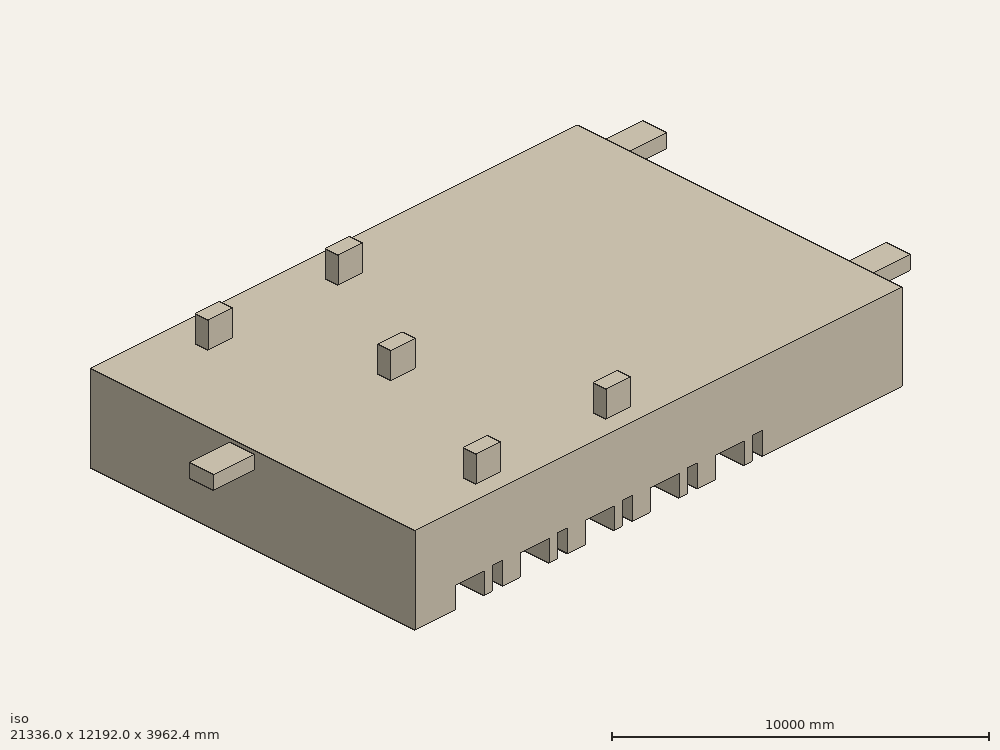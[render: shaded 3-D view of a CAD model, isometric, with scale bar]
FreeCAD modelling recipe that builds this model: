
FCSTD DOCUMENT  (FreeCAD 0.18R14555 (Git shallow))
Label: flow_domain
License: All rights reserved
LicenseURL: http://en.wikipedia.org/wiki/All_rights_reserved
objects: Part::Box×20, Part::MultiFuse×12, Part::Mirroring×1, Part::Cut×1
note: 34 computed .brp shape members not serialized (recipe doc carries the construction recipe); baked Part::Feature solids carry a one-line shape summary decoded from their .brp

FEATURE [Part::Box] Box001  label="Bed 1"
  AttacherType = Attacher::AttachEngine3D
  Height = 762
  Length = 1066.8
  Width = 1981.2
FEATURE [Part::Box] Box002  label="Table 1"
  AttacherType = Attacher::AttachEngine3D
  Height = 798.576
  Length = 396.24
  Placement = pos=(1371.6,0,0) rot=(0,0,1;0rad)
  Width = 396.24
FEATURE [Part::MultiFuse] Fusion  label="Set 1"
  Shapes = -> [Box002,Box001]
FEATURE [Part::Box] Box003  label="Bed 002"
  AttacherType = Attacher::AttachEngine3D
  Height = 762
  Length = 1066.8
  Width = 1981.2
FEATURE [Part::Box] Box004  label="Table 002"
  AttacherType = Attacher::AttachEngine3D
  Height = 798.576
  Length = 396.24
  Placement = pos=(1371.6,0,0) rot=(0,0,1;0rad)
  Width = 396.24
FEATURE [Part::MultiFuse] Fusion001  label="Set 2"
  Placement = pos=(2438.4,0,0) rot=(0,0,1;0rad)
  Shapes = -> [Box004,Box003]
FEATURE [Part::Box] Box005  label="Table 003"
  AttacherType = Attacher::AttachEngine3D
  Height = 798.576
  Length = 396.24
  Placement = pos=(1371.6,0,0) rot=(0,0,1;0rad)
  Width = 396.24
FEATURE [Part::Box] Box006  label="Bed 003"
  AttacherType = Attacher::AttachEngine3D
  Height = 762
  Length = 1066.8
  Width = 1981.2
FEATURE [Part::MultiFuse] Fusion002  label="Set 3"
  Placement = pos=(4876.8,0,0) rot=(0,0,1;0rad)
  Shapes = -> [Box005,Box006]
FEATURE [Part::Box] Box007  label="Bed 004"
  AttacherType = Attacher::AttachEngine3D
  Height = 762
  Length = 1066.8
  Width = 1981.2
FEATURE [Part::Box] Box008  label="Table 004"
  AttacherType = Attacher::AttachEngine3D
  Height = 798.576
  Length = 396.24
  Placement = pos=(1371.6,0,0) rot=(0,0,1;0rad)
  Width = 396.24
FEATURE [Part::MultiFuse] Fusion003  label="Set 4"
  Placement = pos=(7315.2,0,0) rot=(0,0,1;0rad)
  Shapes = -> [Box008,Box007]
FEATURE [Part::Box] Box009  label="Table 005"
  AttacherType = Attacher::AttachEngine3D
  Height = 798.576
  Length = 396.24
  Placement = pos=(1371.6,0,0) rot=(0,0,1;0rad)
  Width = 396.24
FEATURE [Part::Box] Box010  label="Bed 005"
  AttacherType = Attacher::AttachEngine3D
  Height = 762
  Length = 1066.8
  Width = 1981.2
FEATURE [Part::MultiFuse] Fusion004  label="Set 5"
  Placement = pos=(9753.6,0,0) rot=(0,0,1;0rad)
  Shapes = -> [Box009,Box010]
FEATURE [Part::MultiFuse] Fusion005  label="right beds"
  Shapes = -> [Fusion001,Fusion002,Fusion003,Fusion004,Fusion]
FEATURE [Part::Mirroring] Part__Mirroring  label="left beds"
  Base = (0,6096,0)
  Normal = (0,1,0)
  Source = -> Fusion005
FEATURE [Part::Box] Box011  label="Nurse Station"
  AttacherType = Attacher::AttachEngine3D
  Height = 1219.2
  Length = 3048
  Placement = pos=(15240,7620,0) rot=(0,0,1;0rad)
  Width = 4572
FEATURE [Part::Box] Box012  label="main inlet"
  AttacherType = Attacher::AttachEngine3D
  Height = 487.68
  Length = 2438.4
  Placement = pos=(17373.6,1219.2,2438.4) rot=(0,0,1;0rad)
  Width = 914.4
FEATURE [Part::Box] Box013  label="main outlet"
  AttacherType = Attacher::AttachEngine3D
  Height = 487.68
  Length = 2438.4
  Placement = pos=(-1524,6040.43,2438.4) rot=(0,0,1;0rad)
  Width = 914.4
FEATURE [Part::Box] Box016  label="branch002"
  AttacherType = Attacher::AttachEngine3D
  Height = 1219.2
  Length = 914.4
  Placement = pos=(7772.4,609.6,2743.2) rot=(0,0,1;0rad)
  Width = 487.68
FEATURE [Part::Box] Box017  label="branch003"
  AttacherType = Attacher::AttachEngine3D
  Height = 1219.2
  Length = 914.4
  Placement = pos=(7772.4,10668,2743.2) rot=(0,0,1;0rad)
  Width = 487.68
FEATURE [Part::Box] Box018  label="branch004"
  AttacherType = Attacher::AttachEngine3D
  Height = 1219.2
  Length = 914.4
  Placement = pos=(2895.6,609.6,2743.2) rot=(0,0,1;0rad)
  Width = 487.68
FEATURE [Part::Box] Box019  label="branch005"
  AttacherType = Attacher::AttachEngine3D
  Height = 1219.2
  Length = 914.4
  Placement = pos=(2895.6,10668,2743.2) rot=(0,0,1;0rad)
  Width = 487.68
FEATURE [Part::MultiFuse] Fusion006  label="all beds"
  Placement = pos=(1524,0,0) rot=(0,0,1;0rad)
  Shapes = -> [Part__Mirroring,Fusion005]
FEATURE [Part::Box] Box  label="Room"
  AttacherType = Attacher::AttachEngine3D
  Height = 3048
  Length = 18288
  Width = 12192
FEATURE [Part::MultiFuse] Fusion010  label="surfaces"
  Shapes = -> [Fusion006,Box011]
FEATURE [Part::Box] Box020  label="main inlet001"
  AttacherType = Attacher::AttachEngine3D
  Height = 487.68
  Length = 2438.4
  Placement = pos=(17373.6,10363.2,2438.4) rot=(0,0,1;0rad)
  Width = 914.4
FEATURE [Part::MultiFuse] Fusion012  label="main_ducts"
  Shapes = -> [Box020,Box012,Box013]
FEATURE [Part::Box] Box021  label="branch006"
  AttacherType = Attacher::AttachEngine3D
  Height = 1219.2
  Length = 914.4
  Placement = pos=(5181.6,6096,2743.2) rot=(0,0,1;0rad)
  Width = 487.68
FEATURE [Part::MultiFuse] Fusion013
  Shapes = -> [Box016,Box017,Box018,Box019,Box021]
FEATURE [Part::MultiFuse] Fusion014
  Shapes = -> [Fusion012,Fusion013]
FEATURE [Part::MultiFuse] Fusion015
  Shapes = -> [Box,Fusion014]
FEATURE [Part::Cut] Cut
  Base = -> Fusion015
  Tool = -> Fusion010
